# Revit family: Water_Heater-Heat_Pump-Rheem-AMBIHEAT-HDc_270--
name_source: partatom
category: Mechanical Equipment
units: mm (PartAtom-declared; Revit-internal decimal feet)

## family parameters
Always vertical = Yes
Classification = None
Cut with Voids When Loaded = No
OmniClass Number = 23.65.35.11
OmniClass Title = Supply Water Heaters
Part Type = Normal
Room Calculation Point = No
Round Connector Dimension = Use Radius
Shared = No
Work Plane-Based = No

## types (1)
- 270L_551270
    Apparent Power = 985 VA
    Assembly Code = D3020
    Back Wall Clearance Value = 900 mm  [stored 2.95276 ft]
    Barrel Radius = 345 mm  [stored 1.13189 ft]
    Base Height = 41 mm
    Clearance Inside Radius = 358 mm
    Cold Inlet Offset = 122 mm  [stored 0.400262 ft]
    Condensate Outlet Diameter = 13 mm
    Condensate Outlet Radius = 6 mm
    Condensate Outlet Size = 15 mm
    Condensate Outlet Size Radius = 8 mm
    Cover Height = 190 mm
    Cover Vertical Offset = 274 mm  [stored 0.89895 ft]
    Cover Width = 95 mm
    Default Elevation = 0 mm  [stored 0 ft]
    Description = Air Sourced Heat Pump Water Heater
    ENGworks Global = www.ENGWorksGlobal.com
    Frequency = 50 Hz
    Front Wall Clearance Value = 900 mm  [stored 2.95276 ft]
    Hot Outlet Offset = 913 mm
    Inlet Connection Diameter = 19 mm
    Inlet Connection Radius = 10 mm
    Inlet Connection Size = 20 mm
    Inlet Connection Size Radius = 10 mm
    Left Wall Clearance Value = 900 mm  [stored 2.95276 ft]
    Load Classification = HVAC
    Load Sub-Classification Motor = Yes
    Manufacturer = Rheem
    Masking Region Radius = 375 mm
    Minimum Center to Center Installation = 940 mm  [stored 3.08399 ft]
    Minimum Circuit Amps = 15 A
    Minimum Clearance = 250 mm  [stored 0.82021 ft]
    Minimum Clearance Radius = 595 mm  [stored 1.9521 ft]
    Model = HDc-270
    Model Number = 551270
    Number of Poles = 1
    Outlet Connection Diameter = 19 mm
    Outlet Connection Radius = 10 mm
    Outlet Connection Size = 20 mm
    Outlet Connection Size Radius = 10 mm
    Overall Depth = 720 mm  [stored 2.3622 ft]
    Overall Height = 1825 mm  [stored 5.98753 ft]
    Overall Width = 690 mm  [stored 2.26378 ft]
    Product Page URL = https://www.rheem.com.au
    Refrigerant Used = R134a
    Right Wall Clearance Value = 1000 mm  [stored 3.28084 ft]
    Series = AMBIHEAT
    System Performance COP = 4.5
    Tank Material = Metal - Rheem - Gray
    Tank Type = Vitreous Enamel lined
    Temperature Pressure Relief Valve Connection Radius = 6 mm
    Temperature Pressure Relief Valve Diameter = 13 mm
    Temperature Pressure Relief Valve Size = 15 mm
    Temperature Pressure Relief Valve Size Radius = 8 mm
    Top Cover Material = Plastic - Rheem - Dark Gray
    URL = https://www.rheem.com.au
    Unit Weight = 135.00 kgf
    Version = 1
    Voltage = 240 V
    Voltage Comments = 220 VAC - 240 VAC

note: [stored X ft] marks values corroborated as IEEE doubles in the binary element streams (Revit-internal decimal feet)

## geometry (parser evidence)
native form markers: Sweep x3
no freeform markers — native parametric forms only
